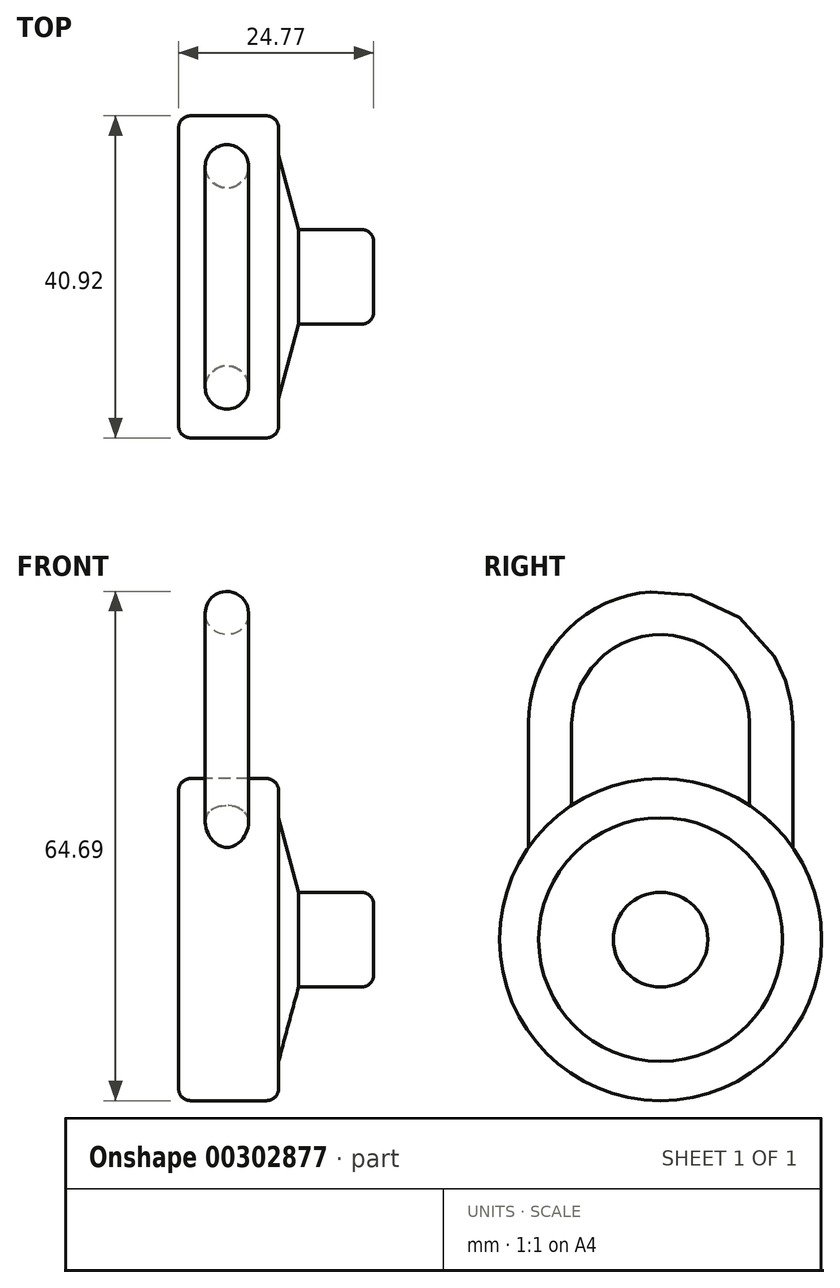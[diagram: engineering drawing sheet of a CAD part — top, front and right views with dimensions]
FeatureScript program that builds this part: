
annotation { "Feature Type Name" : "Feature", "Feature Type Description" : "" }
export const myFeature = defineFeature(function(context is Context, id is Id, definition is map)
    precondition{}
    {
        {
            var Q0;
            Q0=qCreatedBy(makeId("Right.planeOp"),FACE);
            var sketch = newSketch(context, id + "F0", { "sketchPlane" : qUnion([Q0])});
            skCircle(sketch, "E0", {"center": v(0, 0) * mm, "radius": 20.46 * mm});
            skSolve(sketch);
        }
        {
            var Q0;
            Q0=makeQuery(id+"F0.imprint","IMPRINT",FACE,{"disambiguationData":[TD([[makeQuery(id+"F0.imprint","IMPRINT",EDGE,{"derivedFrom":sQuery(id+"F0.wireOp",EDGE,"E0")}),1.0]])]});
            extrude(context, id + "F1", {"entities" : qUnion([Q0]), "depth" : 12.7 * mm});
        }
        {
            var Q0;
            Q0=makeQuery(id+"F1.opExtrude","CAP_FACE",FACE,{"disambiguationData":[OSD([sQuery(id+"F0.wireOp",EDGE,"E0")])],"isStart":false});
            cPlane(context, id + "F2", {"entities" : qUnion([Q0]), "cplaneType" : CPlaneType.OFFSET, "offset" : 6.35 * mm, "oppositeDirection" : true, "width" : 152.4 * mm, "height" : 152.4 * mm});
        }
        {
            var Q0;
            Q0=qCreatedBy(makeId("Top.planeOp"),FACE);
            var sketch = newSketch(context, id + "F3", { "sketchPlane" : qUnion([Q0])});
            skCircle(sketch, "E1", {"center": v(6.14, 14.04) * mm, "radius": 2.75 * mm});
            skSolve(sketch);
        }
        {
            var Q0;
            Q0=qCreatedBy(id+"F2.planeOp",FACE);
            var sketch = newSketch(context, id + "F4", { "sketchPlane" : qUnion([Q0])});
            skLineSegment(sketch, "E2", {"start": v(9.33, 0) * mm, "end": v(9.33, 25.4) * mm});
            skLineSegment(sketch, "E3", {"start": v(0, 0) * mm, "end": v(0, 8.74) * mm});
            skLineSegment(sketch, "E4.MirrorCS", {"start": v(-9.33, 0) * mm, "end": v(-9.33, 25.4) * mm});
            skArc(sketch, "E5", {"start": v(9.33, 25.4) * mm, "mid": v(0, 34.73) * mm, "end": v(-9.33, 25.4) * mm});
            skSolve(sketch);
        }
        {
            var Q0;
            Q0=qCreatedBy(id+"F2.planeOp",FACE);
            var sketch = newSketch(context, id + "F5", { "sketchPlane" : qUnion([Q0])});
            skLineSegment(sketch, "E6.0", {"start": v(11.3, 0) * mm, "end": v(16.79, 0) * mm});
            skLineSegment(sketch, "E7", {"start": v(14.04, 0) * mm, "end": v(14.04, 27.44) * mm});
            skLineSegment(sketch, "E8.MirrorCS", {"start": v(-14.04, 0) * mm, "end": v(-14.04, 27.44) * mm});
            skArc(sketch, "E9", {"start": v(14.04, 27.44) * mm, "mid": v(0, 41.48) * mm, "end": v(-14.04, 27.44) * mm});
            skSolve(sketch);
        }
        {
            var Q0;
            Q0=makeQuery(id+"F3.imprint","IMPRINT",FACE,{"disambiguationData":[TD([[makeQuery(id+"F3.imprint","IMPRINT",EDGE,{"derivedFrom":sQuery(id+"F3.wireOp",EDGE,"E1")}),1.0]])]});
            var Q1;
            Q1=sQuery(id+"F5.wireOp",EDGE,"E7");
            var Q2;
            Q2=sQuery(id+"F5.wireOp",EDGE,"E9");
            var Q3;
            Q3=sQuery(id+"F5.wireOp",EDGE,"E8.MirrorCS");
            sweep(context, id + "F6", {"operationType" : NewBodyOperationType.ADD, "profiles" : qUnion([Q0]), "path" : qUnion([Q1, Q2, Q3])});
        }
        {
            var Q0;
            Q0=makeQuery(id+"F1.opExtrude","CAP_FACE",FACE,{"disambiguationData":[OSD([sQuery(id+"F0.wireOp",EDGE,"E0")])],"isStart":false});
            var sketch = newSketch(context, id + "F7", { "sketchPlane" : qUnion([Q0])});
            skCircle(sketch, "E10", {"center": v(0, 0) * mm, "radius": 15.49 * mm});
            skSolve(sketch);
        }
        {
            var Q0;
            Q0=makeQuery(id+"F7.imprint","IMPRINT",FACE,{"disambiguationData":[TD([[makeQuery(id+"F7.imprint","IMPRINT",EDGE,{"derivedFrom":sQuery(id+"F7.wireOp",EDGE,"E10")}),1.0]])]});
            extrude(context, id + "F8", {"entities" : qUnion([Q0]), "depth" : 2.54 * mm, "hasDraft" : true, "draftAngle" : 75 * degree, "draftPullDirection" : true});
        }
        {
            var Q0;
            Q0=makeQuery(id+"F8.opExtrude","CAP_FACE",FACE,{"disambiguationData":[OSD([sQuery(id+"F7.wireOp",EDGE,"E10")])],"isStart":false});
            extrude(context, id + "F9", {"entities" : qUnion([Q0]), "depth" : 9.52 * mm});
        }
        {
            var Q0;
            Q0=makeQuery(id+"F9.opExtrude","CAP_EDGE",EDGE,{"disambiguationData":[OSD([sQuery(id+"F7.wireOp",EDGE,"E10")])],"isStart":false});
            fillet(context, id + "F10", {"entities" : qUnion([Q0]), "radius" : 1.52 * mm, "tangentPropagation" : true, "allowEdgeOverflow" : false});
        }
        {
            var Q0;
            Q0=makeQuery(id+"F1.opExtrude","CAP_EDGE",EDGE,{"disambiguationData":[OSD([sQuery(id+"F0.wireOp",EDGE,"E0")])],"isStart":true});
            var Q1;
            Q1=makeQuery(id+"F1.opExtrude","CAP_EDGE",EDGE,{"disambiguationData":[OSD([sQuery(id+"F0.wireOp",EDGE,"E0")])],"isStart":false});
            fillet(context, id + "F11", {"entities" : qUnion([Q0, Q1]), "radius" : 1.52 * mm, "tangentPropagation" : true, "allowEdgeOverflow" : false});
        }
    });
